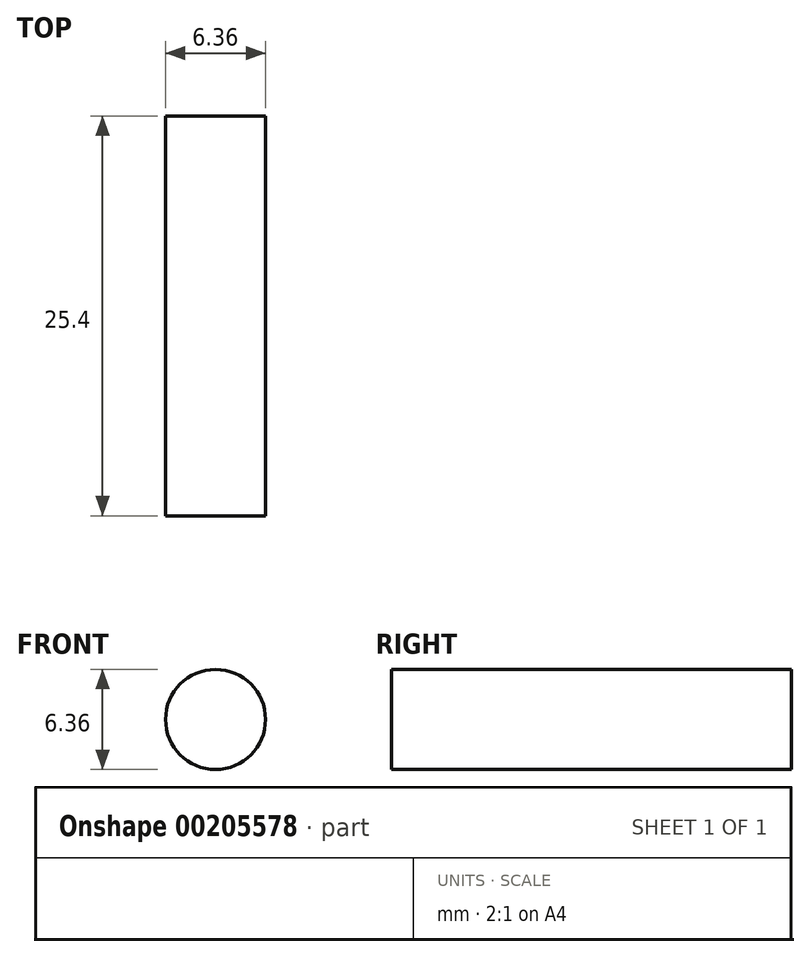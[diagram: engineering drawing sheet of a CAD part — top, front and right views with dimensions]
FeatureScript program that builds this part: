
annotation { "Feature Type Name" : "Feature", "Feature Type Description" : "" }
export const myFeature = defineFeature(function(context is Context, id is Id, definition is map)
    precondition{}
    {
        {
            var Q0;
            Q0=qCreatedBy(makeId("Front.planeOp"),FACE);
            var sketch = newSketch(context, id + "F0", { "sketchPlane" : qUnion([Q0])});
            skCircle(sketch, "E0", {"center": v(0, 0) * mm, "radius": 3.18 * mm});
            skSolve(sketch);
        }
        {
            var Q0;
            Q0=qSketchRegion(id+"F0",true);
            extrude(context, id + "F1", {"entities" : qUnion([Q0]), "flatOperationType" : FlatOperationType.REMOVE, "offsetDistance" : 25.4 * mm, "depth" : 25.4 * mm, "domain" : OperationDomain.MODEL});
        }
    });
